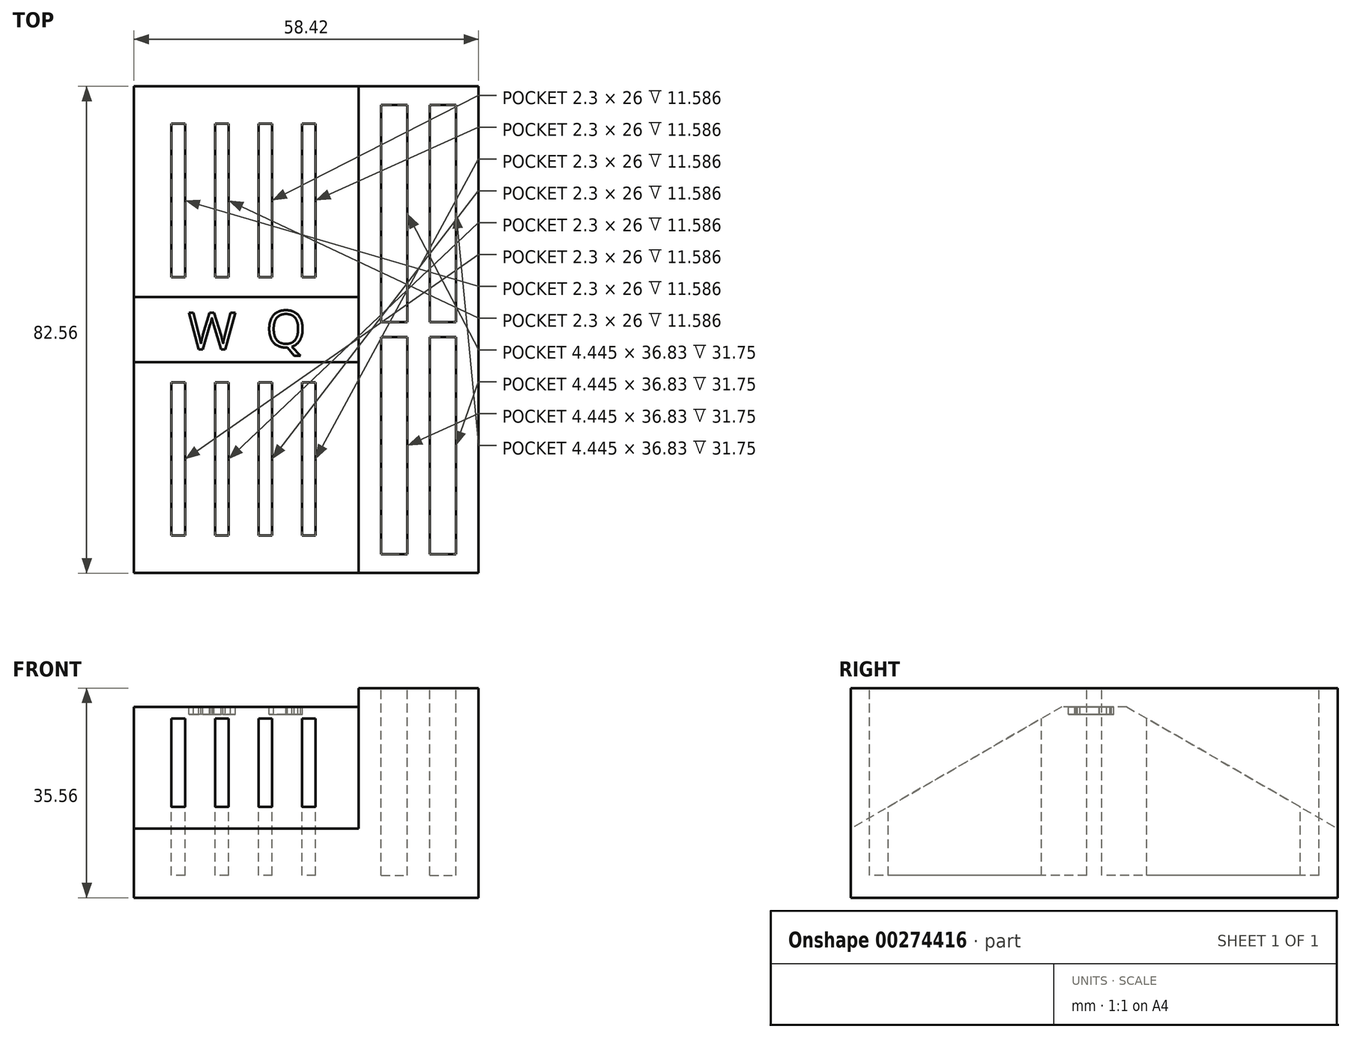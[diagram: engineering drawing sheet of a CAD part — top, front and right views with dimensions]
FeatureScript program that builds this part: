
annotation { "Feature Type Name" : "Feature", "Feature Type Description" : "" }
export const myFeature = defineFeature(function(context is Context, id is Id, definition is map)
    precondition{}
    {
        {
            var Q0;
            Q0=qCreatedBy(makeId("Top.planeOp"),FACE);
            var sketch = newSketch(context, id + "F0", { "sketchPlane" : qUnion([Q0])});
            skLineSegment(sketch, "E0.bottom", {"start": v(-29.2, 41.28) * mm, "end": v(29.21, 41.28) * mm});
            skLineSegment(sketch, "E0.top", {"start": v(-29.21, -41.27) * mm, "end": v(29.2, -41.27) * mm});
            skLineSegment(sketch, "E0.left", {"start": v(-29.2, 41.28) * mm, "end": v(-29.21, -41.27) * mm});
            skLineSegment(sketch, "E0.right", {"start": v(29.21, 41.28) * mm, "end": v(29.2, -41.27) * mm});
            skPoint(sketch, "E0.middle", {"position": v(0, 0) * mm});
            skSolve(sketch);
        }
        {
            var Q0;
            Q0=makeQuery(id+"F0.imprint","IMPRINT",FACE,{"disambiguationData":[TD([[makeQuery(id+"F0.imprint","IMPRINT",EDGE,{"derivedFrom":sQuery(id+"F0.wireOp",EDGE,"E0.bottom")}),-1.0]])]});
            extrude(context, id + "F1", {"entities" : qUnion([Q0]), "depth" : 35.56 * mm});
        }
        {
            var Q0;
            Q0=makeQuery(id+"F1.opExtrude","CAP_FACE",FACE,{"disambiguationData":[OSD([sQuery(id+"F0.wireOp",EDGE,"E0.bottom"),sQuery(id+"F0.wireOp",EDGE,"E0.top"),sQuery(id+"F0.wireOp",EDGE,"E0.left"),sQuery(id+"F0.wireOp",EDGE,"E0.right")])],"isStart":false});
            var sketch = newSketch(context, id + "F2", { "sketchPlane" : qUnion([Q0])});
            skLineSegment(sketch, "E1", {"start": v(-22.86, -8.92) * mm, "end": v(-22.86, -34.92) * mm});
            skLineSegment(sketch, "E2", {"start": v(-22.86, -34.92) * mm, "end": v(-20.56, -34.92) * mm});
            skLineSegment(sketch, "E3", {"start": v(-20.56, -34.92) * mm, "end": v(-20.56, -8.92) * mm});
            skLineSegment(sketch, "E4", {"start": v(-20.56, -8.92) * mm, "end": v(-22.86, -8.92) * mm});
            skLineSegment(sketch, "E5", {"start": v(-15.48, -8.92) * mm, "end": v(-15.48, -34.92) * mm});
            skLineSegment(sketch, "E6", {"start": v(-15.48, -34.92) * mm, "end": v(-13.18, -34.92) * mm});
            skLineSegment(sketch, "E7", {"start": v(-13.18, -34.92) * mm, "end": v(-13.18, -8.92) * mm});
            skLineSegment(sketch, "E8", {"start": v(-13.18, -8.92) * mm, "end": v(-15.48, -8.92) * mm});
            skLineSegment(sketch, "E9", {"start": v(-8.1, -8.92) * mm, "end": v(-8.1, -34.92) * mm});
            skLineSegment(sketch, "E10", {"start": v(-8.1, -34.92) * mm, "end": v(-5.8, -34.92) * mm});
            skLineSegment(sketch, "E11", {"start": v(-5.8, -34.92) * mm, "end": v(-5.8, -8.92) * mm});
            skLineSegment(sketch, "E12", {"start": v(-5.8, -8.92) * mm, "end": v(-8.1, -8.92) * mm});
            skLineSegment(sketch, "E13", {"start": v(-0.72, -8.92) * mm, "end": v(-0.72, -34.92) * mm});
            skLineSegment(sketch, "E14", {"start": v(-0.72, -34.92) * mm, "end": v(1.58, -34.92) * mm});
            skLineSegment(sketch, "E15", {"start": v(1.58, -34.92) * mm, "end": v(1.58, -8.92) * mm});
            skLineSegment(sketch, "E16", {"start": v(1.58, -8.92) * mm, "end": v(-0.72, -8.92) * mm});
            skLineSegment(sketch, "E17", {"start": v(-22.86, 34.93) * mm, "end": v(-22.86, 8.93) * mm});
            skLineSegment(sketch, "E18", {"start": v(-22.86, 8.93) * mm, "end": v(-20.56, 8.93) * mm});
            skLineSegment(sketch, "E19", {"start": v(-20.56, 8.93) * mm, "end": v(-20.56, 34.93) * mm});
            skLineSegment(sketch, "E20", {"start": v(-20.56, 34.93) * mm, "end": v(-22.86, 34.93) * mm});
            skLineSegment(sketch, "E21", {"start": v(-15.48, 34.93) * mm, "end": v(-15.48, 8.93) * mm});
            skLineSegment(sketch, "E22", {"start": v(-15.48, 8.93) * mm, "end": v(-13.18, 8.93) * mm});
            skLineSegment(sketch, "E23", {"start": v(-13.18, 8.93) * mm, "end": v(-13.18, 34.93) * mm});
            skLineSegment(sketch, "E24", {"start": v(-13.18, 34.93) * mm, "end": v(-15.48, 34.93) * mm});
            skLineSegment(sketch, "E25", {"start": v(-8.1, 34.93) * mm, "end": v(-8.1, 8.93) * mm});
            skLineSegment(sketch, "E26", {"start": v(-8.1, 8.93) * mm, "end": v(-5.8, 8.93) * mm});
            skLineSegment(sketch, "E27", {"start": v(-5.8, 8.93) * mm, "end": v(-5.8, 34.93) * mm});
            skLineSegment(sketch, "E28", {"start": v(-5.8, 34.93) * mm, "end": v(-8.1, 34.93) * mm});
            skLineSegment(sketch, "E29", {"start": v(-0.72, 34.93) * mm, "end": v(-0.72, 8.93) * mm});
            skLineSegment(sketch, "E30", {"start": v(-0.72, 8.93) * mm, "end": v(1.58, 8.93) * mm});
            skLineSegment(sketch, "E31", {"start": v(1.58, 8.93) * mm, "end": v(1.58, 34.93) * mm});
            skLineSegment(sketch, "E32", {"start": v(1.58, 34.93) * mm, "end": v(-0.72, 34.93) * mm});
            skSolve(sketch);
        }
        {
            var Q0;
            Q0=makeQuery(id+"F2.imprint","IMPRINT",FACE,{"disambiguationData":[TD([[makeQuery(id+"F2.imprint","IMPRINT",EDGE,{"derivedFrom":sQuery(id+"F2.wireOp",EDGE,"E17")}),1.0]])]});
            var Q1;
            Q1=makeQuery(id+"F2.imprint","IMPRINT",FACE,{"disambiguationData":[TD([[makeQuery(id+"F2.imprint","IMPRINT",EDGE,{"derivedFrom":sQuery(id+"F2.wireOp",EDGE,"E21")}),1.0]])]});
            var Q2;
            Q2=makeQuery(id+"F2.imprint","IMPRINT",FACE,{"disambiguationData":[TD([[makeQuery(id+"F2.imprint","IMPRINT",EDGE,{"derivedFrom":sQuery(id+"F2.wireOp",EDGE,"E25")}),1.0]])]});
            var Q3;
            Q3=makeQuery(id+"F2.imprint","IMPRINT",FACE,{"disambiguationData":[TD([[makeQuery(id+"F2.imprint","IMPRINT",EDGE,{"derivedFrom":sQuery(id+"F2.wireOp",EDGE,"E29")}),1.0]])]});
            var Q4;
            Q4=makeQuery(id+"F2.imprint","IMPRINT",FACE,{"disambiguationData":[TD([[makeQuery(id+"F2.imprint","IMPRINT",EDGE,{"derivedFrom":sQuery(id+"F2.wireOp",EDGE,"E13")}),1.0]])]});
            var Q5;
            Q5=makeQuery(id+"F2.imprint","IMPRINT",FACE,{"disambiguationData":[TD([[makeQuery(id+"F2.imprint","IMPRINT",EDGE,{"derivedFrom":sQuery(id+"F2.wireOp",EDGE,"E9")}),1.0]])]});
            var Q6;
            Q6=makeQuery(id+"F2.imprint","IMPRINT",FACE,{"disambiguationData":[TD([[makeQuery(id+"F2.imprint","IMPRINT",EDGE,{"derivedFrom":sQuery(id+"F2.wireOp",EDGE,"E5")}),1.0]])]});
            var Q7;
            Q7=makeQuery(id+"F2.imprint","IMPRINT",FACE,{"disambiguationData":[TD([[makeQuery(id+"F2.imprint","IMPRINT",EDGE,{"derivedFrom":sQuery(id+"F2.wireOp",EDGE,"E1")}),1.0]])]});
            extrude(context, id + "F3", {"entities" : qUnion([Q0, Q1, Q2, Q3, Q4, Q5, Q6, Q7]), "operationType" : NewBodyOperationType.REMOVE, "oppositeDirection" : true, "depth" : 31.75 * mm});
        }
        {
            var Q0;
            Q0=makeQuery(id+"F1.opExtrude","SWEPT_FACE",FACE,{"disambiguationData":[OSD([sQuery(id+"F0.wireOp",EDGE,"E0.left")])]});
            var sketch = newSketch(context, id + "F4", { "sketchPlane" : qUnion([Q0])});
            skLineSegment(sketch, "E33", {"start": v(0, 35.56) * mm, "end": v(-41.28, 11.73) * mm});
            skLineSegment(sketch, "E34", {"start": v(0, 35.56) * mm, "end": v(41.27, 11.73) * mm});
            skLineSegment(sketch, "E35", {"start": v(-5.53, 32.37) * mm, "end": v(5.53, 32.37) * mm});
            skSolve(sketch);
        }
        {
            var Q0;
            {var subQ0=sQuery(id+"F4.wireOp",EDGE,"E33");Q0=makeQuery(id+"F4.imprint","IMPRINT",FACE,{"disambiguationData":[TD([[makeQuery(id+"F4.imprint","IMPRINT",EDGE,{"derivedFrom":subQ0}),-1.0]])]});}
            var Q1;
            {var subQ0=sQuery(id+"F4.wireOp",EDGE,"E34");Q1=makeQuery(id+"F4.imprint","IMPRINT",FACE,{"disambiguationData":[TD([[makeQuery(id+"F4.imprint","IMPRINT",EDGE,{"derivedFrom":subQ0}),1.0]])]});}
            var Q2;
            {var subQ3=sQuery(id+"F4.wireOp",EDGE,"E35");Q2=makeQuery(id+"F4.imprint","IMPRINT",FACE,{"disambiguationData":[TD([[makeQuery(id+"F4.imprint","IMPRINT",EDGE,{"derivedFrom":subQ3}),1.0]])]});}
            extrude(context, id + "F5", {"entities" : qUnion([Q0, Q1, Q2]), "operationType" : NewBodyOperationType.REMOVE, "oppositeDirection" : true, "depth" : 38.1 * mm});
        }
        {
            var Q0;
            Q0=makeQuery(id+"F1.opExtrude","CAP_FACE",FACE,{"disambiguationData":[OSD([sQuery(id+"F0.wireOp",EDGE,"E0.bottom"),sQuery(id+"F0.wireOp",EDGE,"E0.top"),sQuery(id+"F0.wireOp",EDGE,"E0.left"),sQuery(id+"F0.wireOp",EDGE,"E0.right")])],"isStart":false});
            var sketch = newSketch(context, id + "F6", { "sketchPlane" : qUnion([Q0])});
            skLineSegment(sketch, "E36.bottom", {"start": v(12.7, -1.27) * mm, "end": v(17.15, -1.27) * mm});
            skLineSegment(sketch, "E36.top", {"start": v(12.7, -38.1) * mm, "end": v(17.15, -38.1) * mm});
            skLineSegment(sketch, "E36.left", {"start": v(12.7, -1.27) * mm, "end": v(12.7, -38.1) * mm});
            skLineSegment(sketch, "E36.right", {"start": v(17.15, -1.27) * mm, "end": v(17.15, -38.1) * mm});
            skLineSegment(sketch, "E37.bottom", {"start": v(12.7, 38.1) * mm, "end": v(17.15, 38.1) * mm});
            skLineSegment(sketch, "E37.top", {"start": v(12.7, 1.27) * mm, "end": v(17.15, 1.27) * mm});
            skLineSegment(sketch, "E37.left", {"start": v(12.7, 38.1) * mm, "end": v(12.7, 1.27) * mm});
            skLineSegment(sketch, "E37.right", {"start": v(17.15, 38.1) * mm, "end": v(17.15, 1.27) * mm});
            skLineSegment(sketch, "E38.bottom", {"start": v(20.96, 38.1) * mm, "end": v(25.4, 38.1) * mm});
            skLineSegment(sketch, "E38.top", {"start": v(20.96, 1.27) * mm, "end": v(25.4, 1.27) * mm});
            skLineSegment(sketch, "E38.left", {"start": v(20.96, 38.1) * mm, "end": v(20.96, 1.27) * mm});
            skLineSegment(sketch, "E38.right", {"start": v(25.4, 38.1) * mm, "end": v(25.4, 1.27) * mm});
            skLineSegment(sketch, "E39.bottom", {"start": v(20.96, -1.27) * mm, "end": v(25.4, -1.27) * mm});
            skLineSegment(sketch, "E39.top", {"start": v(20.96, -38.1) * mm, "end": v(25.4, -38.1) * mm});
            skLineSegment(sketch, "E39.left", {"start": v(20.96, -1.27) * mm, "end": v(20.96, -38.1) * mm});
            skLineSegment(sketch, "E39.right", {"start": v(25.4, -1.27) * mm, "end": v(25.4, -38.1) * mm});
            skSolve(sketch);
        }
        {
            var Q0;
            Q0=makeQuery(id+"F6.imprint","IMPRINT",FACE,{"disambiguationData":[TD([[makeQuery(id+"F6.imprint","IMPRINT",EDGE,{"derivedFrom":sQuery(id+"F6.wireOp",EDGE,"E37.bottom")}),-1.0]])]});
            var Q1;
            Q1=makeQuery(id+"F6.imprint","IMPRINT",FACE,{"disambiguationData":[TD([[makeQuery(id+"F6.imprint","IMPRINT",EDGE,{"derivedFrom":sQuery(id+"F6.wireOp",EDGE,"E38.bottom")}),-1.0]])]});
            var Q2;
            Q2=makeQuery(id+"F6.imprint","IMPRINT",FACE,{"disambiguationData":[TD([[makeQuery(id+"F6.imprint","IMPRINT",EDGE,{"derivedFrom":sQuery(id+"F6.wireOp",EDGE,"E36.bottom")}),-1.0]])]});
            var Q3;
            Q3=makeQuery(id+"F6.imprint","IMPRINT",FACE,{"disambiguationData":[TD([[makeQuery(id+"F6.imprint","IMPRINT",EDGE,{"derivedFrom":sQuery(id+"F6.wireOp",EDGE,"E39.bottom")}),-1.0]])]});
            extrude(context, id + "F7", {"entities" : qUnion([Q0, Q1, Q2, Q3]), "operationType" : NewBodyOperationType.REMOVE, "oppositeDirection" : true, "depth" : 31.75 * mm});
        }
        {
            var Q0;
            Q0=makeQuery(id+"F5.boolean.opBoolean","COPY",FACE,{"derivedFrom":makeQuery(id+"F5.opExtrude","SWEPT_FACE",FACE,{"disambiguationData":[OSD([sQuery(id+"F4.wireOp",EDGE,"E35")])]})});
            var sketch = newSketch(context, id + "F8", { "sketchPlane" : qUnion([Q0])});
            skText(sketch, "E40", { "text": "W", "fontName": "OpenSans-Regular.ttf"});
            skText(sketch, "E41", { "text": "Q\n", "fontName": "OpenSans-Regular.ttf"});
            const initialGuessF8  = {"E40": [-0.02004, -0.00333, 1, 0, 0.0063], "E41": [-0.00682, -0.00293, 1, 0, 0.0062]};
            skSetInitialGuess(sketch, initialGuessF8);
            skSolve(sketch);
        }
        {
            var Q0;
            Q0 = qSketchRegion(id + "F8", true);
            extrude(context, id + "F9", {"entities" : qUnion([Q0]), "operationType" : NewBodyOperationType.REMOVE, "oppositeDirection" : true, "depth" : 1.27 * mm});
        }
    });
